# Revit family: H-600_RFA
name_source: partatom
category: Aparatos sanitarios
units: mm (PartAtom-declared; Revit-internal decimal feet)

## family parameters
Compartido = Sí
Corte con vacíos al cargar = No
Cota de conector redondo = Diámetro de uso
Número OmniClass = 23.45.00.00
Punto de cálculo de habitación = No
Se basa en plano de trabajo = No
Siempre vertical = Sí
Tipo de pieza = Normal
Título OmniClass = Sanitary, Laundry, and Cleaning Equipment

## types (1)
- H-600
    Brass Chromed = Brass
    Certification = https://helvex.com.mx
    Comentarios de tipo = Showerheads
    Compliance = NOM-008-CONAGUA-1998
    Data Sheet = https://helvex.com.mx
    Descripción = Fixed Stream Showerhead
    Elevación por defecto = 0"
    Fabricante = HELVEX
    Features = Low, Medium And High Pressure Showerhead; Dynamic Water Economizer; Includes Mobile Node
    Inlet Threads = ½" - 14 NPT
    Max. Water Flow = 2.6 gal/min
    Max. Working Pressure = 85.3 psi
    Min. Water Flow = 1.0 gal/min
    Min. Working Pressure = 2.8 psi
    Modelo = H-600
    URL = https://helvex.com.mx

## geometry (parser evidence)
native form markers: Sweep x3
no freeform markers — native parametric forms only
